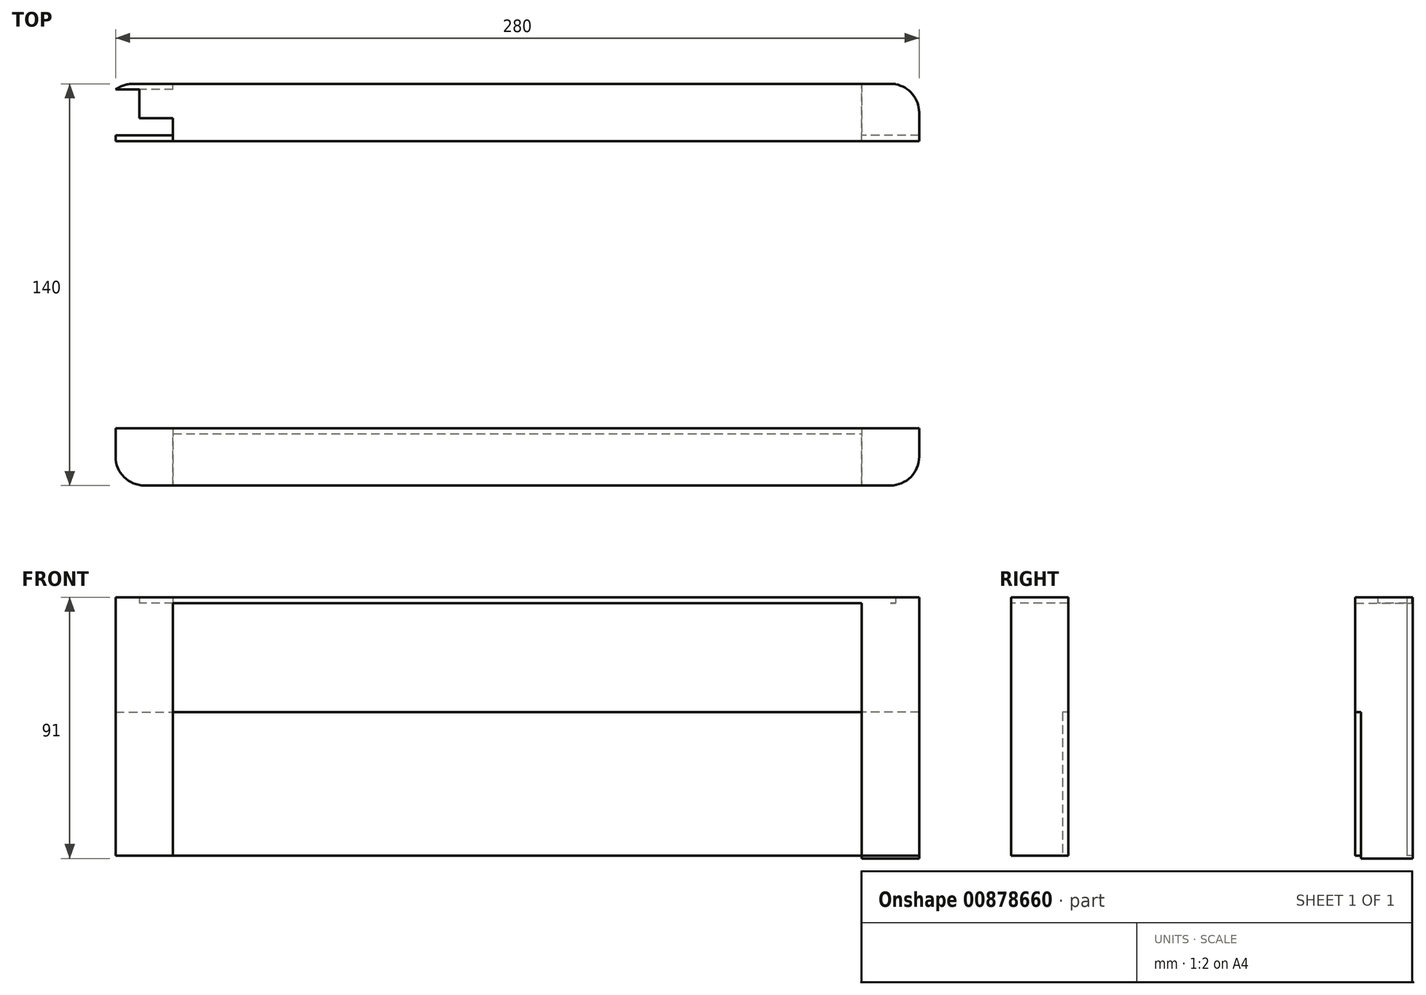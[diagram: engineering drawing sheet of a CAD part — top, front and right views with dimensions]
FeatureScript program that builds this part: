
annotation { "Feature Type Name" : "Feature", "Feature Type Description" : "" }
export const myFeature = defineFeature(function(context is Context, id is Id, definition is map)
    precondition{}
    {
        {
            var Q0;
            Q0=qCreatedBy(makeId("Top.planeOp"),FACE);
            var sketch = newSketch(context, id + "F0", { "sketchPlane" : qUnion([Q0])});
            skLineSegment(sketch, "E0.bottom", {"start": v(140, -70) * mm, "end": v(-140, -70) * mm});
            skLineSegment(sketch, "E0.top", {"start": v(140, 70) * mm, "end": v(-140, 70) * mm});
            skLineSegment(sketch, "E0.left", {"start": v(140, -70) * mm, "end": v(140, 70) * mm});
            skLineSegment(sketch, "E0.right", {"start": v(-140, -70) * mm, "end": v(-140, 70) * mm});
            skPoint(sketch, "E0.middle", {"position": v(0, 0) * mm});
            skLineSegment(sketch, "E1.top", {"start": v(140, 68) * mm, "end": v(-140, 68) * mm});
            skLineSegment(sketch, "E1.left", {"start": v(140, 70) * mm, "end": v(140, 68) * mm});
            skLineSegment(sketch, "E1.right", {"start": v(-140, 70) * mm, "end": v(-140, 68) * mm});
            skLineSegment(sketch, "E2.top", {"start": v(140, -68) * mm, "end": v(-140, -68) * mm});
            skLineSegment(sketch, "E2.left", {"start": v(140, -70) * mm, "end": v(140, -68) * mm});
            skLineSegment(sketch, "E2.right", {"start": v(-140, -70) * mm, "end": v(-140, -68) * mm});
            skLineSegment(sketch, "E3.bottom", {"start": v(-140, 68) * mm, "end": v(-120, 68) * mm});
            skLineSegment(sketch, "E3.top", {"start": v(-140, 50) * mm, "end": v(-120, 50) * mm});
            skLineSegment(sketch, "E3.left", {"start": v(-140, 68) * mm, "end": v(-140, 50) * mm});
            skLineSegment(sketch, "E3.right", {"start": v(-120, 68) * mm, "end": v(-120, 50) * mm});
            skLineSegment(sketch, "E4.MirrorCS", {"start": v(140, 50) * mm, "end": v(120, 50) * mm});
            skLineSegment(sketch, "E5.MirrorCS", {"start": v(120, 68) * mm, "end": v(120, 50) * mm});
            skLineSegment(sketch, "E6.MirrorCS", {"start": v(-140, -50) * mm, "end": v(-120, -50) * mm});
            skLineSegment(sketch, "E7.MirrorCS", {"start": v(-120, -68) * mm, "end": v(-120, -50) * mm});
            skLineSegment(sketch, "E8.MirrorCS", {"start": v(120, -68) * mm, "end": v(120, -50) * mm});
            skLineSegment(sketch, "E9.MirrorCS", {"start": v(140, -50) * mm, "end": v(120, -50) * mm});
            skSolve(sketch);
        }
        {
            var Q0;
            {var subQ3=sQuery(id+"F0.wireOp",EDGE,"E4.MirrorCS");Q0=makeQuery(id+"F0.imprint","IMPRINT",FACE,{"disambiguationData":[TD([[makeQuery(id+"F0.imprint","IMPRINT",EDGE,{"derivedFrom":subQ3}),-1.0]])]});}
            var Q1;
            Q1=makeQuery(id+"F0.imprint","IMPRINT",FACE,{"disambiguationData":[TD([[makeQuery(id+"F0.imprint","IMPRINT",EDGE,{"derivedFrom":sQuery(id+"F0.wireOp",EDGE,"E3.bottom")}),-1.0]])]});
            var Q2;
            Q2=makeQuery(id+"F0.imprint","IMPRINT",FACE,{"disambiguationData":[TD([[makeQuery(id+"F0.imprint","IMPRINT",EDGE,{"derivedFrom":sQuery(id+"F0.wireOp",EDGE,"E0.bottom")}),-1.0]])]});
            var Q3;
            {var subQ3=sQuery(id+"F0.wireOp",EDGE,"E6.MirrorCS");Q3=makeQuery(id+"F0.imprint","IMPRINT",FACE,{"disambiguationData":[TD([[makeQuery(id+"F0.imprint","IMPRINT",EDGE,{"derivedFrom":subQ3}),-1.0]])]});}
            var Q4;
            {var subQ4=sQuery(id+"F0.wireOp",EDGE,"E3.top");Q4=makeQuery(id+"F0.imprint","IMPRINT",FACE,{"disambiguationData":[TD([[makeQuery(id+"F0.imprint","IMPRINT",EDGE,{"derivedFrom":subQ4}),-1.0]])]});}
            var Q5;
            Q5=makeQuery(id+"F0.imprint","IMPRINT",FACE,{"disambiguationData":[TD([[makeQuery(id+"F0.imprint","IMPRINT",EDGE,{"derivedFrom":sQuery(id+"F0.wireOp",EDGE,"E0.top")}),1.0]])]});
            var Q6;
            {var subQ4=sQuery(id+"F0.wireOp",EDGE,"E8.MirrorCS");Q6=makeQuery(id+"F0.imprint","IMPRINT",FACE,{"disambiguationData":[TD([[makeQuery(id+"F0.imprint","IMPRINT",EDGE,{"derivedFrom":subQ4}),-1.0]])]});}
            extrude(context, id + "F1", {"entities" : qUnion([Q0, Q1, Q2, Q3, Q4, Q5, Q6]), "depth" : 1 * mm, "offsetDistance" : 25 * mm});
        }
        {
            var Q0;
            Q0=makeQuery(id+"F1.opExtrude","CAP_FACE",FACE,{"disambiguationData":[OSD([sQuery(id+"F0.wireOp",EDGE,"E0.left"),sQuery(id+"F0.wireOp",EDGE,"E0.right"),sQuery(id+"F0.wireOp",EDGE,"E0.top"),sQuery(id+"F0.wireOp",EDGE,"E1.left"),sQuery(id+"F0.wireOp",EDGE,"E1.right"),sQuery(id+"F0.wireOp",EDGE,"E0.bottom"),sQuery(id+"F0.wireOp",EDGE,"E2.left"),sQuery(id+"F0.wireOp",EDGE,"E2.right"),sQuery(id+"F0.wireOp",EDGE,"E3.left")])],"isStart":false});
            var sketch = newSketch(context, id + "F2", { "sketchPlane" : qUnion([Q0])});
            skLineSegment(sketch, "E10.bottom", {"start": v(-140, -70) * mm, "end": v(-120, -70) * mm});
            skLineSegment(sketch, "E10.top", {"start": v(-140, -52) * mm, "end": v(-120, -52) * mm});
            skLineSegment(sketch, "E10.left", {"start": v(-140, -70) * mm, "end": v(-140, -52) * mm});
            skLineSegment(sketch, "E10.right", {"start": v(-120, -70) * mm, "end": v(-120, -52) * mm});
            skLineSegment(sketch, "E11.MirrorCS", {"start": v(140, -52) * mm, "end": v(120, -52) * mm});
            skLineSegment(sketch, "E12.MirrorCS", {"start": v(120, -70) * mm, "end": v(120, -52) * mm});
            skLineSegment(sketch, "E13.MirrorCS", {"start": v(-140, 52) * mm, "end": v(-120, 52) * mm});
            skLineSegment(sketch, "E14.MirrorCS", {"start": v(-120, 70) * mm, "end": v(-120, 52) * mm});
            skLineSegment(sketch, "E15.MirrorCS", {"start": v(120, 70) * mm, "end": v(120, 52) * mm});
            skLineSegment(sketch, "E16.MirrorCS", {"start": v(140, 52) * mm, "end": v(120, 52) * mm});
            skLineSegment(sketch, "E17.bottom", {"start": v(-140, -52) * mm, "end": v(140, -52) * mm});
            skLineSegment(sketch, "E17.top", {"start": v(-140, -50) * mm, "end": v(140, -50) * mm});
            skLineSegment(sketch, "E17.left", {"start": v(-140, -52) * mm, "end": v(-140, -50) * mm});
            skLineSegment(sketch, "E17.right", {"start": v(140, -52) * mm, "end": v(140, -50) * mm});
            skLineSegment(sketch, "E18.bottom", {"start": v(-140, 52) * mm, "end": v(140, 52) * mm});
            skLineSegment(sketch, "E18.top", {"start": v(-140, 50) * mm, "end": v(140, 50) * mm});
            skLineSegment(sketch, "E18.left", {"start": v(-140, 52) * mm, "end": v(-140, 50) * mm});
            skLineSegment(sketch, "E18.right", {"start": v(140, 52) * mm, "end": v(140, 50) * mm});
            skSolve(sketch);
        }
        {
            var Q0;
            Q0=makeQuery(id+"F2.imprint","IMPRINT",FACE,{"disambiguationData":[TD([[makeQuery(id+"F2.imprint","IMPRINT",EDGE,{"derivedFrom":sQuery(id+"F2.wireOp",EDGE,"E18.top")}),1.0]])]});
            var Q1;
            Q1=makeQuery(id+"F2.imprint","IMPRINT",FACE,{"disambiguationData":[TD([[makeQuery(id+"F2.imprint","IMPRINT",EDGE,{"derivedFrom":sQuery(id+"F2.wireOp",EDGE,"E17.top")}),-1.0]])]});
            extrude(context, id + "F3", {"entities" : qUnion([Q0, Q1]), "operationType" : NewBodyOperationType.ADD, "depth" : 50 * mm, "offsetDistance" : 25 * mm});
        }
        {
            var Q0;
            Q0=makeQuery(id+"F2.imprint","IMPRINT",FACE,{"disambiguationData":[TD([[makeQuery(id+"F2.imprint","IMPRINT",EDGE,{"derivedFrom":sQuery(id+"F2.wireOp",EDGE,"E10.bottom")}),-1.0]])]});
            var Q1;
            {var subQ0=sQuery(id+"F2.wireOp",EDGE,"E12.MirrorCS");Q1=makeQuery(id+"F2.imprint","IMPRINT",FACE,{"disambiguationData":[TD([[makeQuery(id+"F2.imprint","IMPRINT",EDGE,{"derivedFrom":subQ0}),-1.0]])]});}
            var Q2;
            {var subQ0=sQuery(id+"F2.wireOp",EDGE,"E15.MirrorCS");Q2=makeQuery(id+"F2.imprint","IMPRINT",FACE,{"disambiguationData":[TD([[makeQuery(id+"F2.imprint","IMPRINT",EDGE,{"derivedFrom":subQ0}),1.0]])]});}
            var Q3;
            {var subQ0=sQuery(id+"F2.wireOp",EDGE,"E14.MirrorCS");Q3=makeQuery(id+"F2.imprint","IMPRINT",FACE,{"disambiguationData":[TD([[makeQuery(id+"F2.imprint","IMPRINT",EDGE,{"derivedFrom":subQ0}),-1.0]])]});}
            extrude(context, id + "F4", {"entities" : qUnion([Q0, Q1, Q2, Q3]), "operationType" : NewBodyOperationType.ADD, "depth" : 90 * mm, "offsetDistance" : 25 * mm});
        }
        {
            var Q0;
            Q0=makeQuery(id+"F3.opExtrude","CAP_FACE",FACE,{"disambiguationData":[OSD([sQuery(id+"F2.wireOp",EDGE,"E17.bottom"),sQuery(id+"F2.wireOp",EDGE,"E17.top"),sQuery(id+"F2.wireOp",EDGE,"E17.left"),sQuery(id+"F2.wireOp",EDGE,"E17.right")])],"isStart":false});
            var sketch = newSketch(context, id + "F5", { "sketchPlane" : qUnion([Q0])});
            skLineSegment(sketch, "E19.bottom", {"start": v(-140, -50) * mm, "end": v(-120, -50) * mm});
            skLineSegment(sketch, "E19.top", {"start": v(-140, -52) * mm, "end": v(-120, -52) * mm});
            skLineSegment(sketch, "E19.left", {"start": v(-140, -50) * mm, "end": v(-140, -52) * mm});
            skLineSegment(sketch, "E19.right", {"start": v(-120, -50) * mm, "end": v(-120, -52) * mm});
            skLineSegment(sketch, "E20.MirrorCS", {"start": v(120, -50) * mm, "end": v(120, -52) * mm});
            skLineSegment(sketch, "E21.MirrorCS", {"start": v(140, -50) * mm, "end": v(120, -50) * mm});
            skLineSegment(sketch, "E22.MirrorCS", {"start": v(120, 50) * mm, "end": v(120, 52) * mm});
            skLineSegment(sketch, "E23.MirrorCS", {"start": v(140, 50) * mm, "end": v(120, 50) * mm});
            skLineSegment(sketch, "E24.MirrorCS", {"start": v(-120, 50) * mm, "end": v(-120, 52) * mm});
            skLineSegment(sketch, "E25.MirrorCS", {"start": v(-140, 50) * mm, "end": v(-120, 50) * mm});
            skLineSegment(sketch, "E26.bottom", {"start": v(-120, 50) * mm, "end": v(-140, 50) * mm});
            skLineSegment(sketch, "E26.top", {"start": v(-120, 52.05) * mm, "end": v(-140, 52.05) * mm});
            skLineSegment(sketch, "E26.left", {"start": v(-120, 50) * mm, "end": v(-120, 52.05) * mm});
            skLineSegment(sketch, "E26.right", {"start": v(-140, 50) * mm, "end": v(-140, 52.05) * mm});
            skLineSegment(sketch, "E27.top", {"start": v(140, -52) * mm, "end": v(120, -52) * mm});
            skLineSegment(sketch, "E27.left", {"start": v(140, -50) * mm, "end": v(140, -52) * mm});
            skLineSegment(sketch, "E28.top", {"start": v(140, 52) * mm, "end": v(120, 52) * mm});
            skLineSegment(sketch, "E28.left", {"start": v(140, 50) * mm, "end": v(140, 52) * mm});
            skSolve(sketch);
        }
        {
            var Q0;
            Q0=makeQuery(id+"F5.imprint","IMPRINT",FACE,{"disambiguationData":[TD([[makeQuery(id+"F5.imprint","IMPRINT",EDGE,{"derivedFrom":sQuery(id+"F5.wireOp",EDGE,"E19.bottom")}),-1.0]])]});
            var Q1;
            {var subQ0=sQuery(id+"F5.wireOp",EDGE,"E26.bottom");Q1=makeQuery(id+"F5.imprint","IMPRINT",FACE,{"disambiguationData":[TD([[makeQuery(id+"F5.imprint","IMPRINT",EDGE,{"derivedFrom":subQ0}),-1.0]])]});}
            var Q2;
            Q2=makeQuery(id+"F5.imprint","IMPRINT",FACE,{"disambiguationData":[TD([[makeQuery(id+"F5.imprint","IMPRINT",EDGE,{"derivedFrom":sQuery(id+"F5.wireOp",EDGE,"E21.MirrorCS")}),-1.0]])]});
            var Q3;
            Q3=makeQuery(id+"F5.imprint","IMPRINT",FACE,{"disambiguationData":[TD([[makeQuery(id+"F5.imprint","IMPRINT",EDGE,{"derivedFrom":sQuery(id+"F5.wireOp",EDGE,"E23.MirrorCS")}),-1.0]])]});
            extrude(context, id + "F6", {"entities" : qUnion([Q0, Q1, Q2, Q3]), "operationType" : NewBodyOperationType.ADD, "depth" : 40 * mm, "offsetDistance" : 25 * mm});
        }
        {
            var Q0;
            {var subQ0=sQuery(id+"F0.wireOp",EDGE,"E0.bottom");var subQ1=sQuery(id+"F0.wireOp",EDGE,"E3.left");var subQ2=sQuery(id+"F0.wireOp",EDGE,"E2.right");var subQ3=sQuery(id+"F0.wireOp",EDGE,"E1.right");var subQ4=sQuery(id+"F0.wireOp",EDGE,"E0.right");var subQ5=sQuery(id+"F0.wireOp",EDGE,"E2.left");var subQ6=sQuery(id+"F0.wireOp",EDGE,"E1.left");var subQ7=sQuery(id+"F0.wireOp",EDGE,"E0.left");Q0=makeQuery(id+"F3.boolean.opBoolean","SPLIT",FACE,{"disambiguationData":[TD([makeQuery(id+"F1.opExtrude","SWEPT_FACE",FACE,{"disambiguationData":[OSD([subQ0])]})])],"derivedFrom":makeQuery(id+"F1.opExtrude","CAP_FACE",FACE,{"disambiguationData":[OSD([subQ7,subQ4,sQuery(id+"F0.wireOp",EDGE,"E0.top"),subQ6,subQ3,subQ0,subQ5,subQ2,subQ1])],"isStart":false})});}
            var Q1;
            {var subQ0=sQuery(id+"F0.wireOp",EDGE,"E3.left");var subQ1=sQuery(id+"F0.wireOp",EDGE,"E2.right");var subQ2=sQuery(id+"F0.wireOp",EDGE,"E1.right");var subQ3=sQuery(id+"F0.wireOp",EDGE,"E0.right");var subQ4=sQuery(id+"F0.wireOp",EDGE,"E2.left");var subQ5=sQuery(id+"F0.wireOp",EDGE,"E1.left");var subQ6=sQuery(id+"F0.wireOp",EDGE,"E0.left");Q1=makeQuery(id+"F3.boolean.opBoolean","SPLIT",FACE,{"disambiguationData":[TD([makeQuery(id+"F3.opExtrude","SWEPT_FACE",FACE,{"disambiguationData":[OSD([sQuery(id+"F2.wireOp",EDGE,"E17.top")])]})])],"derivedFrom":makeQuery(id+"F1.opExtrude","CAP_FACE",FACE,{"disambiguationData":[OSD([subQ6,subQ3,sQuery(id+"F0.wireOp",EDGE,"E0.top"),subQ5,subQ2,sQuery(id+"F0.wireOp",EDGE,"E0.bottom"),subQ4,subQ1,subQ0])],"isStart":false})});}
            var Q2;
            {var subQ0=sQuery(id+"F0.wireOp",EDGE,"E0.top");var subQ1=sQuery(id+"F0.wireOp",EDGE,"E3.left");var subQ2=sQuery(id+"F0.wireOp",EDGE,"E2.right");var subQ3=sQuery(id+"F0.wireOp",EDGE,"E1.right");var subQ4=sQuery(id+"F0.wireOp",EDGE,"E0.right");var subQ5=sQuery(id+"F0.wireOp",EDGE,"E2.left");var subQ6=sQuery(id+"F0.wireOp",EDGE,"E1.left");var subQ7=sQuery(id+"F0.wireOp",EDGE,"E0.left");Q2=makeQuery(id+"F3.boolean.opBoolean","SPLIT",FACE,{"disambiguationData":[TD([makeQuery(id+"F1.opExtrude","SWEPT_FACE",FACE,{"disambiguationData":[OSD([subQ0])]})])],"derivedFrom":makeQuery(id+"F1.opExtrude","CAP_FACE",FACE,{"disambiguationData":[OSD([subQ7,subQ4,subQ0,subQ6,subQ3,sQuery(id+"F0.wireOp",EDGE,"E0.bottom"),subQ5,subQ2,subQ1])],"isStart":false})});}
            extrude(context, id + "F7", {"entities" : qUnion([Q0, Q1, Q2]), "operationType" : NewBodyOperationType.REMOVE, "oppositeDirection" : true, "depth" : 25 * mm, "offsetDistance" : 25 * mm});
        }
        {
            var Q0;
            {var subQ0=sQuery(id+"F0.wireOp",EDGE,"E0.top");var subQ1=sQuery(id+"F0.wireOp",EDGE,"E2.left");var subQ2=sQuery(id+"F0.wireOp",EDGE,"E1.left");var subQ3=sQuery(id+"F0.wireOp",EDGE,"E0.left");var subQ7=sQuery(id+"F0.wireOp",EDGE,"E3.left");var subQ8=sQuery(id+"F0.wireOp",EDGE,"E2.right");var subQ9=sQuery(id+"F0.wireOp",EDGE,"E1.right");var subQ10=sQuery(id+"F0.wireOp",EDGE,"E0.right");var subQ12=sQuery(id+"F0.wireOp",EDGE,"E0.bottom");Q0=makeQuery(id+"F7.boolean.opBoolean","SPLIT",FACE,{"disambiguationData":[TD([makeQuery(id+"F1.opExtrude","SWEPT_FACE",FACE,{"disambiguationData":[OSD([subQ12])]})])],"derivedFrom":makeQuery(id+"F1.opExtrude","CAP_FACE",FACE,{"disambiguationData":[OSD([subQ3,subQ10,subQ0,subQ2,subQ9,subQ12,subQ1,subQ8,subQ7])],"isStart":true})});}
            var Q1;
            {var subQ0=sQuery(id+"F0.wireOp",EDGE,"E0.top");var subQ2=sQuery(id+"F0.wireOp",EDGE,"E3.left");var subQ3=sQuery(id+"F0.wireOp",EDGE,"E2.right");var subQ4=sQuery(id+"F0.wireOp",EDGE,"E1.right");var subQ5=sQuery(id+"F0.wireOp",EDGE,"E0.right");var subQ9=sQuery(id+"F0.wireOp",EDGE,"E2.left");var subQ10=sQuery(id+"F0.wireOp",EDGE,"E1.left");var subQ11=sQuery(id+"F0.wireOp",EDGE,"E0.left");var subQ14=sQuery(id+"F0.wireOp",EDGE,"E0.bottom");Q1=makeQuery(id+"F7.boolean.opBoolean","SPLIT",FACE,{"disambiguationData":[TD([makeQuery(id+"F1.opExtrude","SWEPT_FACE",FACE,{"disambiguationData":[OSD([subQ0])]})])],"derivedFrom":makeQuery(id+"F1.opExtrude","CAP_FACE",FACE,{"disambiguationData":[OSD([subQ11,subQ5,subQ0,subQ10,subQ4,subQ14,subQ9,subQ3,subQ2])],"isStart":true})});}
            extrude(context, id + "F8", {"entities" : qUnion([Q0, Q1]), "operationType" : NewBodyOperationType.REMOVE, "oppositeDirection" : true, "depth" : 1 * mm, "offsetDistance" : 25 * mm});
        }
        {
            var Q0;
            {var subQ0=sQuery(id+"F2.wireOp",EDGE,"E18.right");var subQ1=sQuery(id+"F2.wireOp",EDGE,"E18.top");var subQ2=sQuery(id+"F0.wireOp",EDGE,"E2.left");var subQ3=sQuery(id+"F0.wireOp",EDGE,"E1.left");var subQ4=sQuery(id+"F0.wireOp",EDGE,"E0.left");Q0=makeQuery(id+"F7.boolean.opBoolean","MERGE",EDGE,{"derivedFrom":[makeQuery(id+"F6.boolean.opBoolean","MERGE",EDGE,{"derivedFrom":[makeQuery(id+"F3.opExtrude","SWEPT_EDGE",EDGE,{"disambiguationData":[OSD([subQ4,subQ3,subQ2,subQ1,subQ0])]}),makeQuery(id+"F6.opExtrude","SWEPT_EDGE",EDGE,{"disambiguationData":[OSD([sQuery(id+"F5.wireOp",EDGE,"E23.MirrorCS"),sQuery(id+"F5.wireOp",EDGE,"E28.left")])]})]})],"fromTools":[makeQuery(id+"F7.opExtrude","SWEPT_EDGE",EDGE,{"disambiguationData":[OSD([subQ4,subQ3,subQ2,subQ1,subQ0])]})]});}
            var Q1;
            {var subQ0=sQuery(id+"F0.wireOp",EDGE,"E1.left");var subQ1=sQuery(id+"F0.wireOp",EDGE,"E0.top");Q1=makeQuery(id+"F4.boolean.opBoolean","MERGE",EDGE,{"derivedFrom":[makeQuery(id+"F1.opExtrude","SWEPT_EDGE",EDGE,{"disambiguationData":[OSD([subQ1,subQ0])]}),makeQuery(id+"F4.opExtrude","SWEPT_EDGE",EDGE,{"disambiguationData":[OSD([sQuery(id+"F0.wireOp",EDGE,"E0.left"),subQ1,subQ0,sQuery(id+"F0.wireOp",EDGE,"E2.left")])]})]});}
            var Q2;
            {var subQ0=sQuery(id+"F0.wireOp",EDGE,"E2.left");var subQ1=sQuery(id+"F0.wireOp",EDGE,"E0.bottom");Q2=makeQuery(id+"F4.boolean.opBoolean","MERGE",EDGE,{"derivedFrom":[makeQuery(id+"F1.opExtrude","SWEPT_EDGE",EDGE,{"disambiguationData":[OSD([subQ1,subQ0])]}),makeQuery(id+"F4.opExtrude","SWEPT_EDGE",EDGE,{"disambiguationData":[OSD([sQuery(id+"F0.wireOp",EDGE,"E0.left"),sQuery(id+"F0.wireOp",EDGE,"E1.left"),subQ1,subQ0])]})]});}
            var Q3;
            {var subQ0=sQuery(id+"F2.wireOp",EDGE,"E17.right");var subQ1=sQuery(id+"F2.wireOp",EDGE,"E17.top");var subQ2=sQuery(id+"F0.wireOp",EDGE,"E2.left");var subQ3=sQuery(id+"F0.wireOp",EDGE,"E1.left");var subQ4=sQuery(id+"F0.wireOp",EDGE,"E0.left");Q3=makeQuery(id+"F7.boolean.opBoolean","MERGE",EDGE,{"derivedFrom":[makeQuery(id+"F6.boolean.opBoolean","MERGE",EDGE,{"derivedFrom":[makeQuery(id+"F3.opExtrude","SWEPT_EDGE",EDGE,{"disambiguationData":[OSD([subQ4,subQ3,subQ2,subQ1,subQ0])]}),makeQuery(id+"F6.opExtrude","SWEPT_EDGE",EDGE,{"disambiguationData":[OSD([sQuery(id+"F5.wireOp",EDGE,"E21.MirrorCS"),sQuery(id+"F5.wireOp",EDGE,"E27.left")])]})]})],"fromTools":[makeQuery(id+"F7.opExtrude","SWEPT_EDGE",EDGE,{"disambiguationData":[OSD([subQ4,subQ3,subQ2,subQ1,subQ0])]})]});}
            var Q4;
            {var subQ0=sQuery(id+"F2.wireOp",EDGE,"E12.MirrorCS");var subQ1=sQuery(id+"F0.wireOp",EDGE,"E0.bottom");Q4=makeQuery(id+"F7.boolean.opBoolean","MERGE",EDGE,{"derivedFrom":[makeQuery(id+"F4.opExtrude","SWEPT_EDGE",EDGE,{"disambiguationData":[OSD([subQ1,subQ0])]})],"fromTools":[makeQuery(id+"F7.opExtrude","SWEPT_EDGE",EDGE,{"disambiguationData":[OSD([subQ1,subQ0])]})]});}
            var Q5;
            {var subQ0=sQuery(id+"F2.wireOp",EDGE,"E15.MirrorCS");var subQ1=sQuery(id+"F0.wireOp",EDGE,"E0.top");Q5=makeQuery(id+"F7.boolean.opBoolean","MERGE",EDGE,{"derivedFrom":[makeQuery(id+"F4.opExtrude","SWEPT_EDGE",EDGE,{"disambiguationData":[OSD([subQ1,subQ0])]})],"fromTools":[makeQuery(id+"F7.opExtrude","SWEPT_EDGE",EDGE,{"disambiguationData":[OSD([subQ1,subQ0])]})]});}
            var Q6;
            {var subQ0=sQuery(id+"F2.wireOp",EDGE,"E14.MirrorCS");var subQ1=sQuery(id+"F0.wireOp",EDGE,"E0.top");Q6=makeQuery(id+"F7.boolean.opBoolean","MERGE",EDGE,{"derivedFrom":[makeQuery(id+"F4.opExtrude","SWEPT_EDGE",EDGE,{"disambiguationData":[OSD([subQ1,subQ0])]})],"fromTools":[makeQuery(id+"F7.opExtrude","SWEPT_EDGE",EDGE,{"disambiguationData":[OSD([subQ1,subQ0])]})]});}
            var Q7;
            {var subQ0=sQuery(id+"F2.wireOp",EDGE,"E18.left");var subQ1=sQuery(id+"F2.wireOp",EDGE,"E18.top");var subQ2=sQuery(id+"F0.wireOp",EDGE,"E3.left");var subQ3=sQuery(id+"F0.wireOp",EDGE,"E2.right");var subQ4=sQuery(id+"F0.wireOp",EDGE,"E1.right");var subQ5=sQuery(id+"F0.wireOp",EDGE,"E0.right");Q7=makeQuery(id+"F7.boolean.opBoolean","MERGE",EDGE,{"derivedFrom":[makeQuery(id+"F6.boolean.opBoolean","MERGE",EDGE,{"derivedFrom":[makeQuery(id+"F3.opExtrude","SWEPT_EDGE",EDGE,{"disambiguationData":[OSD([subQ5,subQ4,subQ3,subQ2,subQ1,subQ0])]}),makeQuery(id+"F6.opExtrude","SWEPT_EDGE",EDGE,{"disambiguationData":[OSD([sQuery(id+"F5.wireOp",EDGE,"E26.bottom"),sQuery(id+"F5.wireOp",EDGE,"E26.right")])]})]})],"fromTools":[makeQuery(id+"F7.opExtrude","SWEPT_EDGE",EDGE,{"disambiguationData":[OSD([subQ5,subQ4,subQ3,subQ2,subQ1,subQ0])]})]});}
            var Q8;
            {var subQ0=sQuery(id+"F0.wireOp",EDGE,"E1.right");var subQ1=sQuery(id+"F0.wireOp",EDGE,"E0.top");Q8=makeQuery(id+"F4.boolean.opBoolean","MERGE",EDGE,{"derivedFrom":[makeQuery(id+"F1.opExtrude","SWEPT_EDGE",EDGE,{"disambiguationData":[OSD([subQ1,subQ0])]}),makeQuery(id+"F4.opExtrude","SWEPT_EDGE",EDGE,{"disambiguationData":[OSD([sQuery(id+"F0.wireOp",EDGE,"E0.right"),subQ1,subQ0,sQuery(id+"F0.wireOp",EDGE,"E2.right"),sQuery(id+"F0.wireOp",EDGE,"E3.left")])]})]});}
            var Q9;
            {var subQ0=sQuery(id+"F2.wireOp",EDGE,"E10.right");var subQ1=sQuery(id+"F2.wireOp",EDGE,"E10.bottom");var subQ2=sQuery(id+"F0.wireOp",EDGE,"E0.bottom");Q9=makeQuery(id+"F7.boolean.opBoolean","MERGE",EDGE,{"derivedFrom":[makeQuery(id+"F4.opExtrude","SWEPT_EDGE",EDGE,{"disambiguationData":[OSD([subQ2,subQ1,subQ0])]})],"fromTools":[makeQuery(id+"F7.opExtrude","SWEPT_EDGE",EDGE,{"disambiguationData":[OSD([subQ2,subQ1,subQ0])]})]});}
            var Q10;
            Q10=makeQuery(id+"F4.boolean.opBoolean","MERGE",EDGE,{"derivedFrom":[makeQuery(id+"F1.opExtrude","SWEPT_EDGE",EDGE,{"disambiguationData":[OSD([sQuery(id+"F0.wireOp",EDGE,"E0.bottom"),sQuery(id+"F0.wireOp",EDGE,"E2.right")])]}),makeQuery(id+"F4.opExtrude","SWEPT_EDGE",EDGE,{"disambiguationData":[OSD([sQuery(id+"F2.wireOp",EDGE,"E10.bottom"),sQuery(id+"F2.wireOp",EDGE,"E10.left")])]})]});
            var Q11;
            {var subQ0=sQuery(id+"F2.wireOp",EDGE,"E17.left");var subQ1=sQuery(id+"F2.wireOp",EDGE,"E17.top");var subQ2=sQuery(id+"F0.wireOp",EDGE,"E3.left");var subQ3=sQuery(id+"F0.wireOp",EDGE,"E2.right");var subQ4=sQuery(id+"F0.wireOp",EDGE,"E1.right");var subQ5=sQuery(id+"F0.wireOp",EDGE,"E0.right");Q11=makeQuery(id+"F7.boolean.opBoolean","MERGE",EDGE,{"derivedFrom":[makeQuery(id+"F6.boolean.opBoolean","MERGE",EDGE,{"derivedFrom":[makeQuery(id+"F3.opExtrude","SWEPT_EDGE",EDGE,{"disambiguationData":[OSD([subQ5,subQ4,subQ3,subQ2,subQ1,subQ0])]}),makeQuery(id+"F6.opExtrude","SWEPT_EDGE",EDGE,{"disambiguationData":[OSD([sQuery(id+"F5.wireOp",EDGE,"E19.bottom"),sQuery(id+"F5.wireOp",EDGE,"E19.left")])]})]})],"fromTools":[makeQuery(id+"F7.opExtrude","SWEPT_EDGE",EDGE,{"disambiguationData":[OSD([subQ5,subQ4,subQ3,subQ2,subQ1,subQ0])]})]});}
            fillet(context, id + "F9", {"entities" : qUnion([Q0, Q1, Q2, Q3, Q4, Q5, Q6, Q7, Q8, Q9, Q10, Q11]), "radius" : 10 * mm, "tangentPropagation" : true, "allowEdgeOverflow" : false});
        }
        {
            var Q0;
            {var subQ0=sQuery(id+"F2.wireOp",EDGE,"E12.MirrorCS");Q0=makeQuery(id+"F7.boolean.opBoolean","MERGE",FACE,{"derivedFrom":[makeQuery(id+"F6.boolean.opBoolean","MERGE",FACE,{"derivedFrom":[makeQuery(id+"F4.opExtrude","SWEPT_FACE",FACE,{"disambiguationData":[OSD([subQ0])]}),makeQuery(id+"F6.opExtrude","SWEPT_FACE",FACE,{"disambiguationData":[OSD([sQuery(id+"F5.wireOp",EDGE,"E20.MirrorCS")])]})]})],"fromTools":[makeQuery(id+"F7.opExtrude","SWEPT_FACE",FACE,{"disambiguationData":[OSD([subQ0])]})]});}
            var sketch = newSketch(context, id + "F10", { "sketchPlane" : qUnion([Q0])});
            skLineSegment(sketch, "E29.bottom", {"start": v(50, 91) * mm, "end": v(70, 91) * mm});
            skLineSegment(sketch, "E29.top", {"start": v(50, 89) * mm, "end": v(70, 89) * mm});
            skLineSegment(sketch, "E29.left", {"start": v(50, 91) * mm, "end": v(50, 89) * mm});
            skLineSegment(sketch, "E29.right", {"start": v(70, 91) * mm, "end": v(70, 89) * mm});
            skLineSegment(sketch, "E30.MirrorCS", {"start": v(-50, 91) * mm, "end": v(-70, 91) * mm});
            skLineSegment(sketch, "E31.MirrorCS", {"start": v(-50, 89) * mm, "end": v(-70, 89) * mm});
            skLineSegment(sketch, "E32.MirrorCS", {"start": v(-50, 91) * mm, "end": v(-50, 89) * mm});
            skLineSegment(sketch, "E33.MirrorCS", {"start": v(-70, 91) * mm, "end": v(-70, 89) * mm});
            skSolve(sketch);
        }
        {
            var Q0;
            {var subQ5=sQuery(id+"F10.wireOp",EDGE,"E29.right");Q0=makeQuery(id+"F10.imprint","IMPRINT",FACE,{"disambiguationData":[TD([[makeQuery(id+"F10.imprint","IMPRINT",EDGE,{"derivedFrom":subQ5}),-1.0]])]});}
            var Q1;
            {var subQ0=sQuery(id+"F10.wireOp",EDGE,"E29.left");Q1=makeQuery(id+"F10.imprint","IMPRINT",FACE,{"disambiguationData":[TD([[makeQuery(id+"F10.imprint","IMPRINT",EDGE,{"derivedFrom":subQ0}),1.0]])]});}
            extrude(context, id + "F11", {"entities" : qUnion([Q0, Q1]), "operationType" : NewBodyOperationType.ADD, "depth" : 240 * mm, "offsetDistance" : 25 * mm});
        }
        {
            var Q0;
            {var subQ0=sQuery(id+"F2.wireOp",EDGE,"E17.bottom");Q0=makeQuery(id+"F11.boolean.opBoolean","MERGE",FACE,{"derivedFrom":[makeQuery(id+"F6.boolean.opBoolean","MERGE",FACE,{"derivedFrom":[makeQuery(id+"F4.opExtrude","CAP_FACE",FACE,{"disambiguationData":[OSD([sQuery(id+"F2.wireOp",EDGE,"E10.bottom"),sQuery(id+"F2.wireOp",EDGE,"E10.left"),sQuery(id+"F2.wireOp",EDGE,"E10.right"),subQ0])],"isStart":false}),makeQuery(id+"F6.opExtrude","CAP_FACE",FACE,{"disambiguationData":[OSD([sQuery(id+"F5.wireOp",EDGE,"E19.bottom"),sQuery(id+"F5.wireOp",EDGE,"E19.top"),sQuery(id+"F5.wireOp",EDGE,"E19.left"),sQuery(id+"F5.wireOp",EDGE,"E19.right")])],"isStart":false})]}),makeQuery(id+"F6.boolean.opBoolean","MERGE",FACE,{"derivedFrom":[makeQuery(id+"F4.opExtrude","CAP_FACE",FACE,{"disambiguationData":[OSD([sQuery(id+"F0.wireOp",EDGE,"E0.left"),sQuery(id+"F0.wireOp",EDGE,"E1.left"),sQuery(id+"F0.wireOp",EDGE,"E0.bottom"),sQuery(id+"F0.wireOp",EDGE,"E2.left"),sQuery(id+"F2.wireOp",EDGE,"E12.MirrorCS"),subQ0])],"isStart":false}),makeQuery(id+"F6.opExtrude","CAP_FACE",FACE,{"disambiguationData":[OSD([sQuery(id+"F5.wireOp",EDGE,"E21.MirrorCS"),sQuery(id+"F5.wireOp",EDGE,"E27.top"),sQuery(id+"F5.wireOp",EDGE,"E27.left"),sQuery(id+"F5.wireOp",EDGE,"E20.MirrorCS")])],"isStart":false})]}),makeQuery(id+"F11.opExtrude","SWEPT_FACE",FACE,{"disambiguationData":[OSD([sQuery(id+"F10.wireOp",EDGE,"E29.bottom")])]})]});}
            var sketch = newSketch(context, id + "F12", { "sketchPlane" : qUnion([Q0])});
            skLineSegment(sketch, "E34.bottom", {"start": v(120, -70) * mm, "end": v(131.78, -70) * mm});
            skLineSegment(sketch, "E34.top", {"start": v(120, -57.96) * mm, "end": v(131.78, -57.96) * mm});
            skLineSegment(sketch, "E34.left", {"start": v(120, -70) * mm, "end": v(120, -57.96) * mm});
            skLineSegment(sketch, "E34.right", {"start": v(131.78, -70) * mm, "end": v(131.78, -57.96) * mm});
            skLineSegment(sketch, "E35.MirrorCS", {"start": v(-120, -57.96) * mm, "end": v(-131.78, -57.96) * mm});
            skLineSegment(sketch, "E36.MirrorCS", {"start": v(-131.78, -70) * mm, "end": v(-131.78, -57.96) * mm});
            skLineSegment(sketch, "E37.MirrorCS", {"start": v(-120, -70) * mm, "end": v(-131.78, -70) * mm});
            skLineSegment(sketch, "E38.MirrorCS", {"start": v(-120, -70) * mm, "end": v(-120, -57.96) * mm});
            skLineSegment(sketch, "E39.MirrorCS", {"start": v(-120, 57.96) * mm, "end": v(-131.78, 57.96) * mm});
            skLineSegment(sketch, "E40.MirrorCS", {"start": v(-131.78, 70) * mm, "end": v(-131.78, 57.96) * mm});
            skLineSegment(sketch, "E41.MirrorCS", {"start": v(-120, 70) * mm, "end": v(-131.78, 70) * mm});
            skLineSegment(sketch, "E42.MirrorCS", {"start": v(-120, 70) * mm, "end": v(-120, 57.96) * mm});
            skLineSegment(sketch, "E43.MirrorCS", {"start": v(131.78, 70) * mm, "end": v(131.78, 57.96) * mm});
            skLineSegment(sketch, "E44.MirrorCS", {"start": v(120, 70) * mm, "end": v(120, 57.96) * mm});
            skLineSegment(sketch, "E45.MirrorCS", {"start": v(120, 70) * mm, "end": v(131.78, 70) * mm});
            skLineSegment(sketch, "E46.MirrorCS", {"start": v(120, 57.96) * mm, "end": v(131.78, 57.96) * mm});
            skSolve(sketch);
        }
        {
            var Q0;
            {var subQ0=sQuery(id+"F12.wireOp",EDGE,"E38.MirrorCS");var subQ1=sQuery(id+"F12.wireOp",EDGE,"E37.MirrorCS");var subQ2=makeQuery(id+"F12.imprint","INTERSECT",VERTEX,{"derivedFrom":[makeQuery(id+"F11.opExtrude","SWEPT_EDGE",EDGE,{"disambiguationData":[OSD([sQuery(id+"F10.wireOp",EDGE,"E29.bottom"),sQuery(id+"F10.wireOp",EDGE,"E29.right")])]}),subQ1,subQ0]});Q0=makeQuery(id+"F12.imprint","IMPRINT",FACE,{"disambiguationData":[TD([[makeQuery(id+"F12.imprint","IMPRINT",EDGE,{"disambiguationData":[TD([[subQ2,-1.0]])],"derivedFrom":subQ1}),-1.0]])]});}
            var Q1;
            {var subQ0=sQuery(id+"F12.wireOp",EDGE,"E34.left");var subQ1=sQuery(id+"F12.wireOp",EDGE,"E34.bottom");var subQ2=makeQuery(id+"F12.imprint","INTERSECT",VERTEX,{"derivedFrom":[makeQuery(id+"F11.opExtrude","SWEPT_EDGE",EDGE,{"disambiguationData":[OSD([sQuery(id+"F10.wireOp",EDGE,"E29.bottom"),sQuery(id+"F10.wireOp",EDGE,"E29.right")])]}),subQ1,subQ0]});Q1=makeQuery(id+"F12.imprint","IMPRINT",FACE,{"disambiguationData":[TD([[makeQuery(id+"F12.imprint","IMPRINT",EDGE,{"disambiguationData":[TD([[subQ2,-1.0]])],"derivedFrom":subQ1}),1.0]])]});}
            extrude(context, id + "F13", {"entities" : qUnion([Q0, Q1]), "operationType" : NewBodyOperationType.ADD, "oppositeDirection" : true, "depth" : 2 * mm, "offsetDistance" : 25 * mm});
        }
        {
            var Q0;
            Q0=makeQuery(id+"F10.imprint","IMPRINT",FACE,{"disambiguationData":[TD([[makeQuery(id+"F10.imprint","IMPRINT",EDGE,{"derivedFrom":sQuery(id+"F10.wireOp",EDGE,"E30.MirrorCS")}),1.0]])]});
            extrude(context, id + "F14", {"entities" : qUnion([Q0]), "operationType" : NewBodyOperationType.ADD, "depth" : 240 * mm, "offsetDistance" : 25 * mm});
        }
        {
            var Q0;
            Q0=makeQuery(id+"F12.imprint","IMPRINT",FACE,{"disambiguationData":[TD([[makeQuery(id+"F12.imprint","IMPRINT",EDGE,{"derivedFrom":sQuery(id+"F12.wireOp",EDGE,"E43.MirrorCS")}),-1.0]])]});
            var Q1;
            Q1=makeQuery(id+"F12.imprint","IMPRINT",FACE,{"disambiguationData":[TD([[makeQuery(id+"F12.imprint","IMPRINT",EDGE,{"derivedFrom":sQuery(id+"F12.wireOp",EDGE,"E39.MirrorCS")}),-1.0]])]});
            extrude(context, id + "F15", {"entities" : qUnion([Q0, Q1]), "operationType" : NewBodyOperationType.ADD, "oppositeDirection" : true, "depth" : 2 * mm, "offsetDistance" : 25 * mm});
        }
    });
